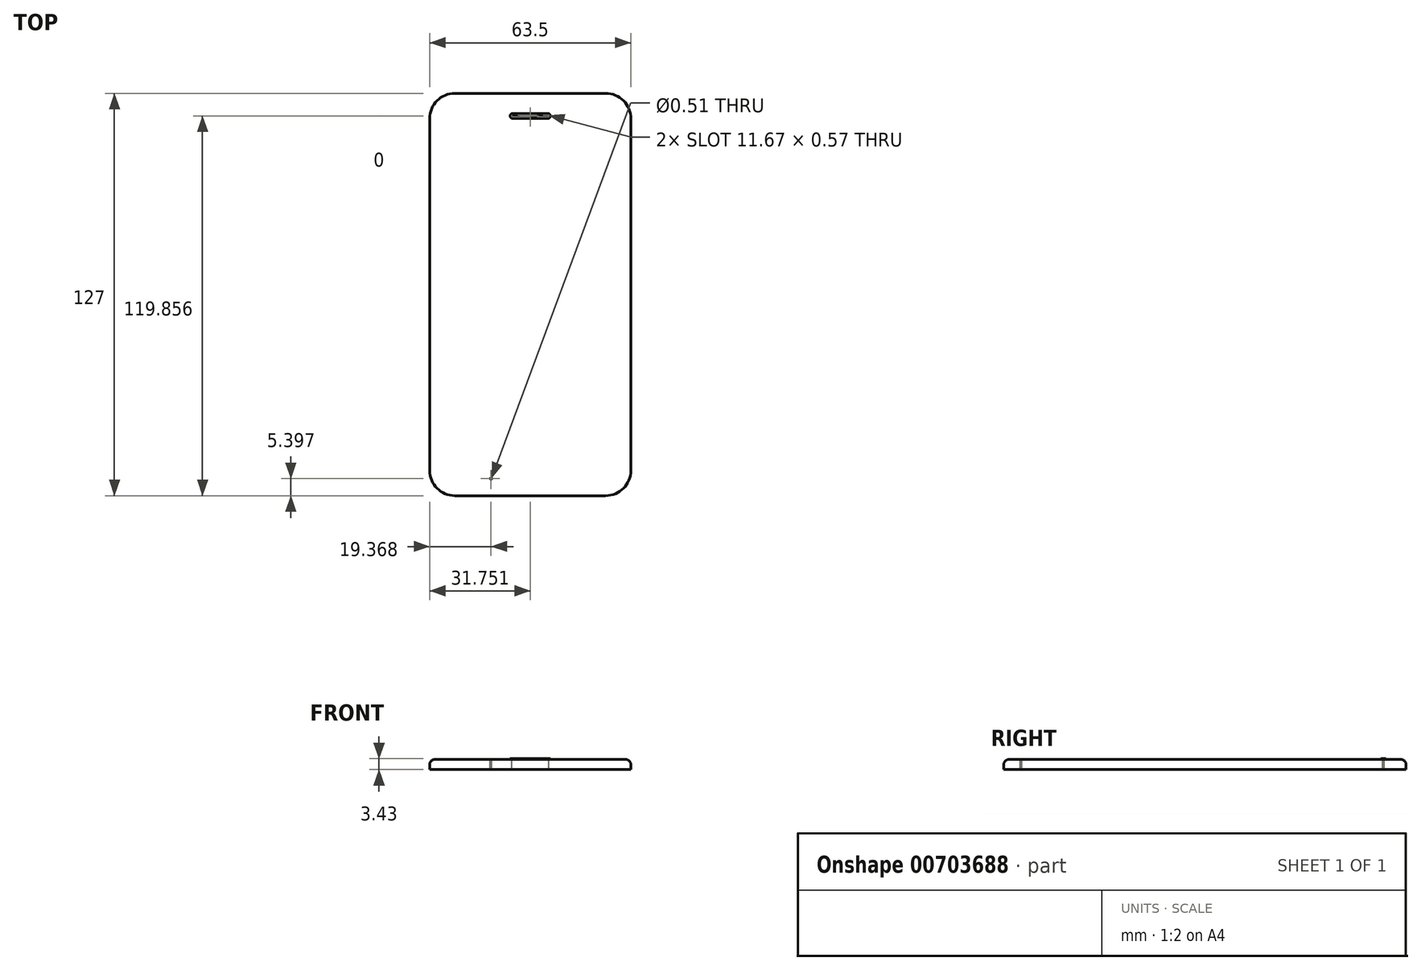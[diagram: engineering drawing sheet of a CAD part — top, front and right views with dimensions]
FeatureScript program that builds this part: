
annotation { "Feature Type Name" : "Feature", "Feature Type Description" : "" }
export const myFeature = defineFeature(function(context is Context, id is Id, definition is map)
    precondition{}
    {
        {
            var Q0;
            Q0=qCreatedBy(makeId("Top.planeOp"),FACE);
            var sketch = newSketch(context, id + "F0", { "sketchPlane" : qUnion([Q0])});
            skLineSegment(sketch, "E0.bottom", {"start": v(-19.36, 62.96) * mm, "end": v(28.26, 62.96) * mm});
            skLineSegment(sketch, "E0.top", {"start": v(-19.36, -64.04) * mm, "end": v(28.26, -64.04) * mm});
            skLineSegment(sketch, "E0.left", {"start": v(-27.3, 55.02) * mm, "end": v(-27.3, -56.1) * mm});
            skLineSegment(sketch, "E0.right", {"start": v(36.2, 55.02) * mm, "end": v(36.2, -56.1) * mm});
            skPoint(sketch, "E1.visualSharp", {"position": v(-27.3, 62.96) * mm});
            skArc(sketch, "E1.filletArc", {"start": v(-19.36, 62.96) * mm, "mid": v(-24.97, 60.63) * mm, "end": v(-27.3, 55.02) * mm});
            skPoint(sketch, "E2.visualSharp", {"position": v(36.2, 62.96) * mm});
            skArc(sketch, "E2.filletArc", {"start": v(36.2, 55.02) * mm, "mid": v(33.88, 60.63) * mm, "end": v(28.26, 62.96) * mm});
            skPoint(sketch, "E3.visualSharp", {"position": v(36.2, -64.04) * mm});
            skArc(sketch, "E3.filletArc", {"start": v(28.26, -64.04) * mm, "mid": v(33.88, -61.72) * mm, "end": v(36.2, -56.1) * mm});
            skPoint(sketch, "E4.visualSharp", {"position": v(-27.3, -64.04) * mm});
            skArc(sketch, "E4.filletArc", {"start": v(-27.3, -56.1) * mm, "mid": v(-24.97, -61.72) * mm, "end": v(-19.36, -64.04) * mm});
            skSolve(sketch);
        }
        {
            var Q0;
            Q0 = qSketchRegion(id + "F0", true);
            extrude(context, id + "F1", {"entities" : qUnion([Q0]), "depth" : 3.17 * mm, "offsetDistance" : 25.4 * mm});
        }
        {
            var Q0;
            Q0=makeQuery(id+"F1.opExtrude","CAP_EDGE",EDGE,{"disambiguationData":[OSD([sQuery(id+"F0.wireOp",EDGE,"E0.right")])],"isStart":false});
            var Q1;
            Q1=makeQuery(id+"F1.opExtrude","CAP_EDGE",EDGE,{"disambiguationData":[OSD([sQuery(id+"F0.wireOp",EDGE,"E2.filletArc")])],"isStart":false});
            var Q2;
            Q2=makeQuery(id+"F1.opExtrude","CAP_EDGE",EDGE,{"disambiguationData":[OSD([sQuery(id+"F0.wireOp",EDGE,"E0.bottom")])],"isStart":false});
            var Q3;
            Q3=makeQuery(id+"F1.opExtrude","CAP_EDGE",EDGE,{"disambiguationData":[OSD([sQuery(id+"F0.wireOp",EDGE,"E1.filletArc")])],"isStart":false});
            var Q4;
            Q4=makeQuery(id+"F1.opExtrude","CAP_EDGE",EDGE,{"disambiguationData":[OSD([sQuery(id+"F0.wireOp",EDGE,"E0.left")])],"isStart":false});
            var Q5;
            Q5=makeQuery(id+"F1.opExtrude","CAP_EDGE",EDGE,{"disambiguationData":[OSD([sQuery(id+"F0.wireOp",EDGE,"E4.filletArc")])],"isStart":false});
            var Q6;
            Q6=makeQuery(id+"F1.opExtrude","CAP_EDGE",EDGE,{"disambiguationData":[OSD([sQuery(id+"F0.wireOp",EDGE,"E0.top")])],"isStart":false});
            var Q7;
            Q7=makeQuery(id+"F1.opExtrude","CAP_EDGE",EDGE,{"disambiguationData":[OSD([sQuery(id+"F0.wireOp",EDGE,"E3.filletArc")])],"isStart":false});
            var Q8;
            Q8=makeQuery(id+"F1.opExtrude","CAP_FACE",FACE,{"disambiguationData":[OSD([sQuery(id+"F0.wireOp",EDGE,"E0.bottom"),sQuery(id+"F0.wireOp",EDGE,"E0.top"),sQuery(id+"F0.wireOp",EDGE,"E0.left"),sQuery(id+"F0.wireOp",EDGE,"E0.right"),sQuery(id+"F0.wireOp",EDGE,"E1.filletArc"),sQuery(id+"F0.wireOp",EDGE,"E2.filletArc"),sQuery(id+"F0.wireOp",EDGE,"E3.filletArc"),sQuery(id+"F0.wireOp",EDGE,"E4.filletArc")])],"isStart":false});
            fillet(context, id + "F2", {"entities" : qUnion([Q0, Q1, Q2, Q3, Q4, Q5, Q6, Q7, Q8]), "radius" : 1.59 * mm, "tangentPropagation" : true, "allowEdgeOverflow" : false});
        }
        {
            var Q0;
            Q0=makeQuery(id+"F1.opExtrude","CAP_FACE",FACE,{"disambiguationData":[OSD([sQuery(id+"F0.wireOp",EDGE,"E0.bottom"),sQuery(id+"F0.wireOp",EDGE,"E0.top"),sQuery(id+"F0.wireOp",EDGE,"E0.left"),sQuery(id+"F0.wireOp",EDGE,"E0.right"),sQuery(id+"F0.wireOp",EDGE,"E1.filletArc"),sQuery(id+"F0.wireOp",EDGE,"E2.filletArc"),sQuery(id+"F0.wireOp",EDGE,"E3.filletArc"),sQuery(id+"F0.wireOp",EDGE,"E4.filletArc")])],"isStart":false});
            var sketch = newSketch(context, id + "F3", { "sketchPlane" : qUnion([Q0])});
            skLineSegment(sketch, "E5.bottom", {"start": v(-1.1, 56.6) * mm, "end": v(10, 56.6) * mm});
            skLineSegment(sketch, "E5.top", {"start": v(-1.1, 55.02) * mm, "end": v(10, 55.02) * mm});
            skLineSegment(sketch, "E5.left", {"start": v(-1.9, 55.82) * mm, "end": v(-1.9, 55.8) * mm});
            skLineSegment(sketch, "E5.right", {"start": v(10.8, 55.82) * mm, "end": v(10.8, 55.8) * mm});
            skPoint(sketch, "E6.visualSharp", {"position": v(-1.9, 55.02) * mm});
            skArc(sketch, "E6.filletArc", {"start": v(-1.9, 55.82) * mm, "mid": v(-1.66, 55.26) * mm, "end": v(-1.1, 55.02) * mm});
            skPoint(sketch, "E7.visualSharp", {"position": v(-1.9, 56.6) * mm});
            skArc(sketch, "E7.filletArc", {"start": v(-1.1, 56.6) * mm, "mid": v(-1.66, 56.38) * mm, "end": v(-1.9, 55.8) * mm});
            skPoint(sketch, "E8.visualSharp", {"position": v(10.8, 56.6) * mm});
            skArc(sketch, "E8.filletArc", {"start": v(10.8, 55.8) * mm, "mid": v(10.57, 56.38) * mm, "end": v(10, 56.6) * mm});
            skPoint(sketch, "E9.visualSharp", {"position": v(10.8, 55.02) * mm});
            skArc(sketch, "E9.filletArc", {"start": v(10, 55.02) * mm, "mid": v(10.57, 55.26) * mm, "end": v(10.8, 55.82) * mm});
            skLineSegment(sketch, "E10", {"start": v(-1.1, 56.1) * mm, "end": v(10, 56.1) * mm});
            skLineSegment(sketch, "E11", {"start": v(-1.1, 55.53) * mm, "end": v(10, 55.53) * mm});
            skLineSegment(sketch, "E12", {"start": v(-1.1, 56.6) * mm, "end": v(-1.1, 55.02) * mm, "construction": true});
            skArc(sketch, "E13", {"start": v(-1.1, 56.1) * mm, "mid": v(-1.38, 55.82) * mm, "end": v(-1.1, 55.53) * mm});
            skArc(sketch, "E14", {"start": v(10, 55.53) * mm, "mid": v(10.29, 55.82) * mm, "end": v(10, 56.1) * mm});
            skLineSegment(sketch, "E15.0", {"start": v(28.26, 61.37) * mm, "end": v(-19.36, 61.37) * mm, "construction": true});
            skPoint(sketch, "E16", {"position": v(4.45, 56.6) * mm});
            skPoint(sketch, "E17.0", {"position": v(4.45, 61.37) * mm});
            skSolve(sketch);
        }
        {
            var Q0;
            Q0=makeQuery(id+"F3.imprint","IMPRINT",FACE,{"disambiguationData":[TD([[makeQuery(id+"F3.imprint","IMPRINT",EDGE,{"derivedFrom":sQuery(id+"F3.wireOp",EDGE,"E10")}),-1.0]])]});
            extrude(context, id + "F4", {"entities" : qUnion([Q0]), "operationType" : NewBodyOperationType.REMOVE, "endBound" : BoundingType.THROUGH_ALL, "oppositeDirection" : true, "depth" : 2.54 * mm, "offsetDistance" : 25.4 * mm});
        }
        {
            var Q0;
            Q0 = qSketchRegion(id + "F3", true);
            extrude(context, id + "F5", {"entities" : qUnion([Q0]), "operationType" : NewBodyOperationType.ADD, "depth" : 0.25 * mm, "offsetDistance" : 25.4 * mm});
        }
        {
            var Q0;
            Q0=makeQuery(id+"F1.opExtrude","CAP_FACE",FACE,{"disambiguationData":[OSD([sQuery(id+"F0.wireOp",EDGE,"E0.bottom"),sQuery(id+"F0.wireOp",EDGE,"E0.top"),sQuery(id+"F0.wireOp",EDGE,"E0.left"),sQuery(id+"F0.wireOp",EDGE,"E0.right"),sQuery(id+"F0.wireOp",EDGE,"E1.filletArc"),sQuery(id+"F0.wireOp",EDGE,"E2.filletArc"),sQuery(id+"F0.wireOp",EDGE,"E3.filletArc"),sQuery(id+"F0.wireOp",EDGE,"E4.filletArc")])],"isStart":false});
            var sketch = newSketch(context, id + "F6", { "sketchPlane" : qUnion([Q0])});
            skLineSegment(sketch, "E18", {"start": v(10.8, 55.8) * mm, "end": v(43.9, 55.8) * mm, "construction": true});
            skCircle(sketch, "E19", {"center": v(26.68, 55.8) * mm, "radius": 1.59 * mm});
            skSolve(sketch);
        }
        {
            var Q0;
            Q0=sQuery(id+"F6.wireOp",EDGE,"E19");
            extrude(context, id + "F7", {"bodyType" : ToolBodyType.SURFACE, "surfaceEntities" : qUnion([Q0]), "depth" : 0.25 * mm, "offsetDistance" : 25.4 * mm});
        }
        {
            var Q0;
            Q0=makeQuery(id+"F1.opExtrude","CAP_FACE",FACE,{"disambiguationData":[OSD([sQuery(id+"F0.wireOp",EDGE,"E0.bottom"),sQuery(id+"F0.wireOp",EDGE,"E0.top"),sQuery(id+"F0.wireOp",EDGE,"E0.left"),sQuery(id+"F0.wireOp",EDGE,"E0.right"),sQuery(id+"F0.wireOp",EDGE,"E1.filletArc"),sQuery(id+"F0.wireOp",EDGE,"E2.filletArc"),sQuery(id+"F0.wireOp",EDGE,"E3.filletArc"),sQuery(id+"F0.wireOp",EDGE,"E4.filletArc")])],"isStart":false});
            var sketch = newSketch(context, id + "F8", { "sketchPlane" : qUnion([Q0])});
            skCircle(sketch, "E20", {"center": v(-7.93, -58.64) * mm, "radius": 0.25 * mm});
            skSolve(sketch);
        }
        {
            var Q0;
            Q0 = qSketchRegion(id + "F8", true);
            extrude(context, id + "F9", {"entities" : qUnion([Q0]), "operationType" : NewBodyOperationType.REMOVE, "endBound" : BoundingType.THROUGH_ALL, "oppositeDirection" : true, "depth" : 25.4 * mm, "offsetDistance" : 25.4 * mm});
        }
    });
